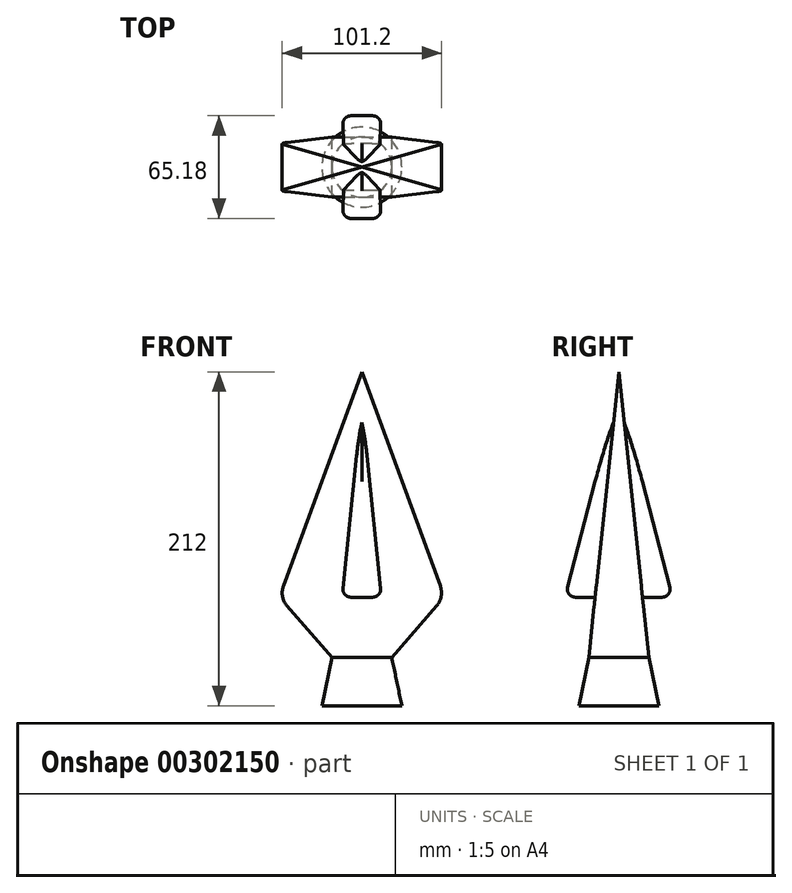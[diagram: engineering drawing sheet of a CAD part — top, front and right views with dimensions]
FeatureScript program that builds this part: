
annotation { "Feature Type Name" : "Feature", "Feature Type Description" : "" }
export const myFeature = defineFeature(function(context is Context, id is Id, definition is map)
    precondition{}
    {
        {
            var Q0;
            Q0=qCreatedBy(makeId("Front.planeOp"),FACE);
            var sketch = newSketch(context, id + "F0", { "sketchPlane" : qUnion([Q0])});
            skLineSegment(sketch, "E0", {"start": v(-52.4, -58.97) * mm, "end": v(0, 84.13) * mm});
            skLineSegment(sketch, "E1", {"start": v(0, 84.13) * mm, "end": v(52.4, -58.97) * mm});
            skLineSegment(sketch, "E2", {"start": v(-52.4, -58.97) * mm, "end": v(-19.05, -97.28) * mm});
            skLineSegment(sketch, "E3", {"start": v(-19.05, -97.28) * mm, "end": v(19.05, -97.28) * mm});
            skLineSegment(sketch, "E4", {"start": v(19.05, -97.28) * mm, "end": v(52.4, -58.97) * mm});
            skSolve(sketch);
        }
        {
            var Q0;
            Q0 = qSketchRegion(id + "F0", true);
            extrude(context, id + "F1", {"entities" : qUnion([Q0]), "endBound" : BoundingType.SYMMETRIC, "depth" : 38.1 * mm});
        }
        {
            var Q0;
            Q0=qCreatedBy(makeId("Front.planeOp"),FACE);
            var sketch = newSketch(context, id + "F2", { "sketchPlane" : qUnion([Q0])});
            skLineSegment(sketch, "E5", {"start": v(19.05, -97.28) * mm, "end": v(25.4, -127.87) * mm});
            skLineSegment(sketch, "E6", {"start": v(0, -97.28) * mm, "end": v(19.05, -97.28) * mm});
            skLineSegment(sketch, "E7", {"start": v(25.4, -127.87) * mm, "end": v(0, -127.87) * mm});
            skLineSegment(sketch, "E8", {"start": v(0, 0) * mm, "end": v(0, -167.27) * mm});
            skSolve(sketch);
        }
        {
            var Q0;
            Q0=makeQuery(id+"F2.imprint","IMPRINT",FACE,{"disambiguationData":[TD([[makeQuery(id+"F2.imprint","IMPRINT",EDGE,{"derivedFrom":sQuery(id+"F2.wireOp",EDGE,"E5")}),-1.0]])]});
            var Q1;
            Q1=sQuery(id+"F2.wireOp",EDGE,"E5");
            var Q2;
            Q2=sQuery(id+"F2.wireOp",EDGE,"E7");
            var Q3;
            Q3=sQuery(id+"F2.wireOp",EDGE,"E6");
            var Q4;
            Q4=sQuery(id+"F2.wireOp",EDGE,"E8");
            revolve(context, id + "F3", {"operationType" : NewBodyOperationType.ADD, "entities" : qUnion([Q0]), "surfaceEntities" : qUnion([Q1, Q2, Q3]), "axis" : qUnion([Q4]), "revolveType" : RevolveType.FULL});
        }
        {
            var Q0;
            Q0=qCreatedBy(makeId("Front.planeOp"),FACE);
            var sketch = newSketch(context, id + "F4", { "sketchPlane" : qUnion([Q0])});
            skLineSegment(sketch, "E9.0", {"start": v(25.4, -127.87) * mm, "end": v(0, -127.87) * mm});
            skLineSegment(sketch, "E10.0", {"start": v(-25.4, -127.87) * mm, "end": v(25.4, -127.87) * mm});
            skLineSegment(sketch, "E11", {"start": v(25.4, -127.87) * mm, "end": v(25.4, -204.07) * mm});
            skSolve(sketch);
        }
        {
            var Q0;
            Q0=sQuery(id+"F4.wireOp",EDGE,"E11");
            var Q1;
            Q1=sQuery(id+"F2.wireOp",EDGE,"E8");
            revolve(context, id + "F5", {"bodyType" : ToolBodyType.SURFACE, "surfaceEntities" : qUnion([Q0]), "axis" : qUnion([Q1]), "revolveType" : RevolveType.FULL});
        }
        {
            var Q0;
            Q0=qCreatedBy(makeId("Right.planeOp"),FACE);
            var sketch = newSketch(context, id + "F6", { "sketchPlane" : qUnion([Q0])});
            skPoint(sketch, "E12.0", {"position": v(-19.05, -97.28) * mm});
            skPoint(sketch, "E13.0", {"position": v(19.05, -97.28) * mm});
            skPoint(sketch, "E14.0", {"position": v(0, 84.13) * mm});
            skLineSegment(sketch, "E15", {"start": v(-19.05, -97.28) * mm, "end": v(0, 84.13) * mm});
            skLineSegment(sketch, "E16", {"start": v(19.05, -97.28) * mm, "end": v(0, 84.13) * mm});
            skLineSegment(sketch, "E17.0", {"start": v(-19.05, 84.13) * mm, "end": v(-19.05, -58.97) * mm});
            skLineSegment(sketch, "E18.0", {"start": v(-19.05, 84.13) * mm, "end": v(19.05, 84.13) * mm});
            skLineSegment(sketch, "E19.0", {"start": v(19.05, 84.13) * mm, "end": v(19.05, -58.97) * mm});
            skLineSegment(sketch, "E20", {"start": v(-19.05, -97.28) * mm, "end": v(-19.05, 84.13) * mm});
            skLineSegment(sketch, "E21", {"start": v(19.05, 84.13) * mm, "end": v(19.05, -97.28) * mm});
            skSolve(sketch);
        }
        {
            var Q0;
            Q0 = qSketchRegion(id + "F6", true);
            extrude(context, id + "F7", {"entities" : qUnion([Q0]), "operationType" : NewBodyOperationType.REMOVE, "endBound" : BoundingType.THROUGH_ALL, "oppositeDirection" : true, "depth" : 127 * mm});
        }
        {
            var Q0;
            Q0 = qSketchRegion(id + "F6", true);
            extrude(context, id + "F8", {"entities" : qUnion([Q0]), "operationType" : NewBodyOperationType.REMOVE, "endBound" : BoundingType.THROUGH_ALL, "depth" : 25.4 * mm});
        }
        {
            var Q0;
            Q0=qCreatedBy(makeId("Right.planeOp"),FACE);
            var sketch = newSketch(context, id + "F9", { "sketchPlane" : qUnion([Q0])});
            skLineSegment(sketch, "E22.0.0", {"start": v(0, 84.13) * mm, "end": v(-15.03, -58.97) * mm});
            skLineSegment(sketch, "E22.0.1", {"start": v(-15.03, -58.97) * mm, "end": v(-19.05, -97.28) * mm});
            skLineSegment(sketch, "E22.0.4", {"start": v(-19.05, -97.28) * mm, "end": v(-15.03, -58.97) * mm});
            skLineSegment(sketch, "E23.0.0", {"start": v(15.03, -58.97) * mm, "end": v(0, 84.13) * mm});
            skLineSegment(sketch, "E23.0.2", {"start": v(-15.03, -58.97) * mm, "end": v(15.03, -58.97) * mm});
            skLineSegment(sketch, "E24.0.1", {"start": v(-19.05, -97.28) * mm, "end": v(0, -97.28) * mm});
            skLineSegment(sketch, "E24.0.2", {"start": v(0, -97.28) * mm, "end": v(19.05, -97.28) * mm});
            skLineSegment(sketch, "E24.0.3", {"start": v(19.05, -97.28) * mm, "end": v(15.03, -58.97) * mm});
            skLineSegment(sketch, "E24.0.4", {"start": v(15.03, -58.97) * mm, "end": v(-15.03, -58.97) * mm});
            skLineSegment(sketch, "E25.0.1", {"start": v(0, 84.13) * mm, "end": v(15.03, -58.97) * mm});
            skLineSegment(sketch, "E25.0.2", {"start": v(15.03, -58.97) * mm, "end": v(19.05, -97.28) * mm});
            skLineSegment(sketch, "E26", {"start": v(-2.12, 63.94) * mm, "end": v(-34.08, -58.97) * mm});
            skLineSegment(sketch, "E27", {"start": v(-34.08, -58.97) * mm, "end": v(-15.03, -58.97) * mm});
            skSolve(sketch);
        }
        {
            var Q0;
            {var subQ2=sQuery(id+"F9.wireOp",EDGE,"E26");Q0=makeQuery(id+"F9.imprint","IMPRINT",FACE,{"disambiguationData":[TD([[makeQuery(id+"F9.imprint","IMPRINT",EDGE,{"derivedFrom":subQ2}),1.0]])]});}
            extrude(context, id + "F10", {"entities" : qUnion([Q0]), "endBound" : BoundingType.SYMMETRIC, "depth" : 25.4 * mm});
        }
        {
            var Q0;
            Q0=qCreatedBy(makeId("Right.planeOp"),FACE);
            var sketch = newSketch(context, id + "F11", { "sketchPlane" : qUnion([Q0])});
            skLineSegment(sketch, "E28.0.0", {"start": v(-2.12, 63.94) * mm, "end": v(-34.08, -58.97) * mm});
            skLineSegment(sketch, "E28.0.2", {"start": v(-34.08, -58.97) * mm, "end": v(-2.12, 63.94) * mm});
            skLineSegment(sketch, "E29.0.0", {"start": v(15.03, -58.97) * mm, "end": v(0, 84.13) * mm});
            skLineSegment(sketch, "E29.0.1", {"start": v(0, 84.13) * mm, "end": v(15.03, -58.97) * mm});
            skLineSegment(sketch, "E29.0.2", {"start": v(15.03, -58.97) * mm, "end": v(19.05, -97.28) * mm});
            skLineSegment(sketch, "E29.0.5", {"start": v(19.05, -97.28) * mm, "end": v(15.03, -58.97) * mm});
            skLineSegment(sketch, "E30", {"start": v(2.12, 63.94) * mm, "end": v(34.08, -58.97) * mm});
            skLineSegment(sketch, "E31", {"start": v(34.08, -58.97) * mm, "end": v(15.03, -58.97) * mm});
            skSolve(sketch);
        }
        {
            var Q0;
            Q0 = qSketchRegion(id + "F11", true);
            extrude(context, id + "F12", {"entities" : qUnion([Q0]), "endBound" : BoundingType.SYMMETRIC, "depth" : 25.4 * mm});
        }
        {
            var Q0;
            Q0=makeQuery(id+"F10.opExtrude","SWEPT_FACE",FACE,{"disambiguationData":[OSD([sQuery(id+"F9.wireOp",EDGE,"E26")])]});
            var sketch = newSketch(context, id + "F13", { "sketchPlane" : qUnion([Q0])});
            skLineSegment(sketch, "E32.0.0", {"start": v(-12.7, 61.35) * mm, "end": v(-12.7, -65.65) * mm, "construction": true});
            skLineSegment(sketch, "E32.0.1", {"start": v(-12.7, -65.65) * mm, "end": v(12.7, -65.65) * mm, "construction": true});
            skLineSegment(sketch, "E32.0.2", {"start": v(12.7, -65.65) * mm, "end": v(12.7, 61.35) * mm, "construction": true});
            skLineSegment(sketch, "E32.0.3", {"start": v(12.7, 61.35) * mm, "end": v(-12.7, 61.35) * mm, "construction": true});
            skLineSegment(sketch, "E33", {"start": v(-12.7, -65.65) * mm, "end": v(0, 61.35) * mm, "construction": true});
            skLineSegment(sketch, "E34", {"start": v(0, 61.35) * mm, "end": v(12.7, -65.65) * mm, "construction": true});
            skLineSegment(sketch, "E35", {"start": v(-12.7, 61.35) * mm, "end": v(-12.7, -65.65) * mm});
            skLineSegment(sketch, "E36", {"start": v(-12.7, 61.35) * mm, "end": v(0, 61.35) * mm});
            skLineSegment(sketch, "E37", {"start": v(0, 61.35) * mm, "end": v(12.7, -65.65) * mm});
            skLineSegment(sketch, "E38", {"start": v(0, 61.35) * mm, "end": v(12.7, 61.35) * mm});
            skLineSegment(sketch, "E39", {"start": v(12.7, 61.35) * mm, "end": v(12.7, -65.65) * mm});
            skLineSegment(sketch, "E40", {"start": v(0, 61.35) * mm, "end": v(-12.7, -65.65) * mm});
            skSolve(sketch);
        }
        {
            var Q0;
            Q0=makeQuery(id+"F13.imprint","IMPRINT",FACE,{"disambiguationData":[TD([[makeQuery(id+"F13.imprint","IMPRINT",EDGE,{"derivedFrom":sQuery(id+"F13.wireOp",EDGE,"E37")}),1.0]])]});
            var Q1;
            Q1=makeQuery(id+"F13.imprint","IMPRINT",FACE,{"disambiguationData":[TD([[makeQuery(id+"F13.imprint","IMPRINT",EDGE,{"derivedFrom":sQuery(id+"F13.wireOp",EDGE,"E35")}),1.0]])]});
            var Q2;
            {var subQ0=sQuery(id+"F6.wireOp",EDGE,"E15");Q2=makeQuery(id+"F8.boolean.opBoolean","MERGE",FACE,{"derivedFrom":[makeQuery(id+"F7.boolean.opBoolean","COPY",FACE,{"derivedFrom":makeQuery(id+"F7.opExtrude","SWEPT_FACE",FACE,{"disambiguationData":[OSD([subQ0])]})}),makeQuery(id+"F8.opExtrude","SWEPT_FACE",FACE,{"disambiguationData":[OSD([subQ0])]})]});}
            extrude(context, id + "F14", {"entities" : qUnion([Q0, Q1]), "operationType" : NewBodyOperationType.REMOVE, "endBound" : BoundingType.UP_TO_SURFACE, "oppositeDirection" : true, "endBoundEntityFace" : qUnion([Q2]), "depth" : 25.4 * mm});
        }
        {
            var Q0;
            Q0=makeQuery(id+"F12.opExtrude","SWEPT_FACE",FACE,{"disambiguationData":[OSD([sQuery(id+"F11.wireOp",EDGE,"E30")])]});
            var sketch = newSketch(context, id + "F15", { "sketchPlane" : qUnion([Q0])});
            skLineSegment(sketch, "E41.0.0", {"start": v(12.7, -65.65) * mm, "end": v(12.7, 61.35) * mm});
            skLineSegment(sketch, "E41.0.1", {"start": v(12.7, 61.35) * mm, "end": v(-12.7, 61.35) * mm});
            skLineSegment(sketch, "E41.0.2", {"start": v(-12.7, 61.35) * mm, "end": v(-12.7, -65.65) * mm});
            skLineSegment(sketch, "E41.0.3", {"start": v(-12.7, -65.65) * mm, "end": v(12.7, -65.65) * mm});
            skLineSegment(sketch, "E42", {"start": v(-12.7, -65.65) * mm, "end": v(0, 61.35) * mm});
            skLineSegment(sketch, "E43", {"start": v(0, 61.35) * mm, "end": v(12.7, -65.65) * mm});
            skLineSegment(sketch, "E44", {"start": v(12.7, 61.35) * mm, "end": v(0, 61.35) * mm});
            skLineSegment(sketch, "E45", {"start": v(0, 61.35) * mm, "end": v(-12.7, 61.35) * mm});
            skLineSegment(sketch, "E46", {"start": v(-12.7, -65.65) * mm, "end": v(-12.7, 61.35) * mm});
            skLineSegment(sketch, "E47", {"start": v(12.7, 61.35) * mm, "end": v(12.7, -65.65) * mm});
            skSolve(sketch);
        }
        {
            var Q0;
            Q0=makeQuery(id+"F15.imprint","IMPRINT",FACE,{"disambiguationData":[TD([[makeQuery(id+"F15.imprint","IMPRINT",EDGE,{"derivedFrom":sQuery(id+"F15.wireOp",EDGE,"E43")}),1.0]])]});
            var Q1;
            Q1=makeQuery(id+"F15.imprint","IMPRINT",FACE,{"disambiguationData":[TD([[makeQuery(id+"F15.imprint","IMPRINT",EDGE,{"derivedFrom":sQuery(id+"F15.wireOp",EDGE,"E42")}),1.0]])]});
            var Q2;
            {var subQ0=sQuery(id+"F6.wireOp",EDGE,"E16");Q2=makeQuery(id+"F8.boolean.opBoolean","MERGE",FACE,{"derivedFrom":[makeQuery(id+"F7.boolean.opBoolean","COPY",FACE,{"derivedFrom":makeQuery(id+"F7.opExtrude","SWEPT_FACE",FACE,{"disambiguationData":[OSD([subQ0])]})}),makeQuery(id+"F8.opExtrude","SWEPT_FACE",FACE,{"disambiguationData":[OSD([subQ0])]})]});}
            extrude(context, id + "F16", {"entities" : qUnion([Q0, Q1]), "operationType" : NewBodyOperationType.REMOVE, "endBound" : BoundingType.UP_TO_SURFACE, "oppositeDirection" : true, "endBoundEntityFace" : qUnion([Q2]), "depth" : 25.4 * mm});
        }
        {
            var Q0;
            Q0=makeQuery(id+"F1.opExtrude","SWEPT_EDGE",EDGE,{"disambiguationData":[OSD([sQuery(id+"F0.wireOp",EDGE,"E0"),sQuery(id+"F0.wireOp",EDGE,"E2")])]});
            var Q1;
            Q1=makeQuery(id+"F1.opExtrude","SWEPT_EDGE",EDGE,{"disambiguationData":[OSD([sQuery(id+"F0.wireOp",EDGE,"E1"),sQuery(id+"F0.wireOp",EDGE,"E4")])]});
            fillet(context, id + "F17", {"entities" : qUnion([Q0, Q1]), "radius" : 12.7 * mm, "tangentPropagation" : true, "allowEdgeOverflow" : false});
        }
        {
            var Q0;
            Q0=makeQuery(id+"F12.opExtrude","SWEPT_FACE",FACE,{"disambiguationData":[OSD([sQuery(id+"F11.wireOp",EDGE,"E30")])]});
            var Q1;
            Q1=makeQuery(id+"F16.boolean.opBoolean","INTERSECT",EDGE,{"derivedFrom":[makeQuery(id+"F12.opExtrude","SWEPT_FACE",FACE,{"disambiguationData":[OSD([sQuery(id+"F11.wireOp",EDGE,"E31")])]}),makeQuery(id+"F16.opExtrude","SWEPT_FACE",FACE,{"disambiguationData":[OSD([sQuery(id+"F15.wireOp",EDGE,"E42")])]})]});
            var Q2;
            Q2=makeQuery(id+"F16.boolean.opBoolean","INTERSECT",EDGE,{"derivedFrom":[makeQuery(id+"F12.opExtrude","SWEPT_FACE",FACE,{"disambiguationData":[OSD([sQuery(id+"F11.wireOp",EDGE,"E31")])]}),makeQuery(id+"F16.opExtrude","SWEPT_FACE",FACE,{"disambiguationData":[OSD([sQuery(id+"F15.wireOp",EDGE,"E43")])]})]});
            fillet(context, id + "F18", {"entities" : qUnion([Q0, Q1, Q2]), "radius" : 5.08 * mm, "tangentPropagation" : true, "allowEdgeOverflow" : false});
        }
        {
            var Q0;
            Q0=makeQuery(id+"F10.opExtrude","SWEPT_FACE",FACE,{"disambiguationData":[OSD([sQuery(id+"F9.wireOp",EDGE,"E26")])]});
            var Q1;
            Q1=makeQuery(id+"F14.boolean.opBoolean","INTERSECT",EDGE,{"derivedFrom":[makeQuery(id+"F10.opExtrude","SWEPT_FACE",FACE,{"disambiguationData":[OSD([sQuery(id+"F9.wireOp",EDGE,"E27")])]}),makeQuery(id+"F14.opExtrude","SWEPT_FACE",FACE,{"disambiguationData":[OSD([sQuery(id+"F13.wireOp",EDGE,"E37")])]})]});
            var Q2;
            Q2=makeQuery(id+"F14.boolean.opBoolean","INTERSECT",EDGE,{"derivedFrom":[makeQuery(id+"F10.opExtrude","SWEPT_FACE",FACE,{"disambiguationData":[OSD([sQuery(id+"F9.wireOp",EDGE,"E27")])]}),makeQuery(id+"F14.opExtrude","SWEPT_FACE",FACE,{"disambiguationData":[OSD([sQuery(id+"F13.wireOp",EDGE,"E40")])]})]});
            fillet(context, id + "F19", {"entities" : qUnion([Q0, Q1, Q2]), "radius" : 5.08 * mm, "tangentPropagation" : true, "allowEdgeOverflow" : false});
        }
    });
